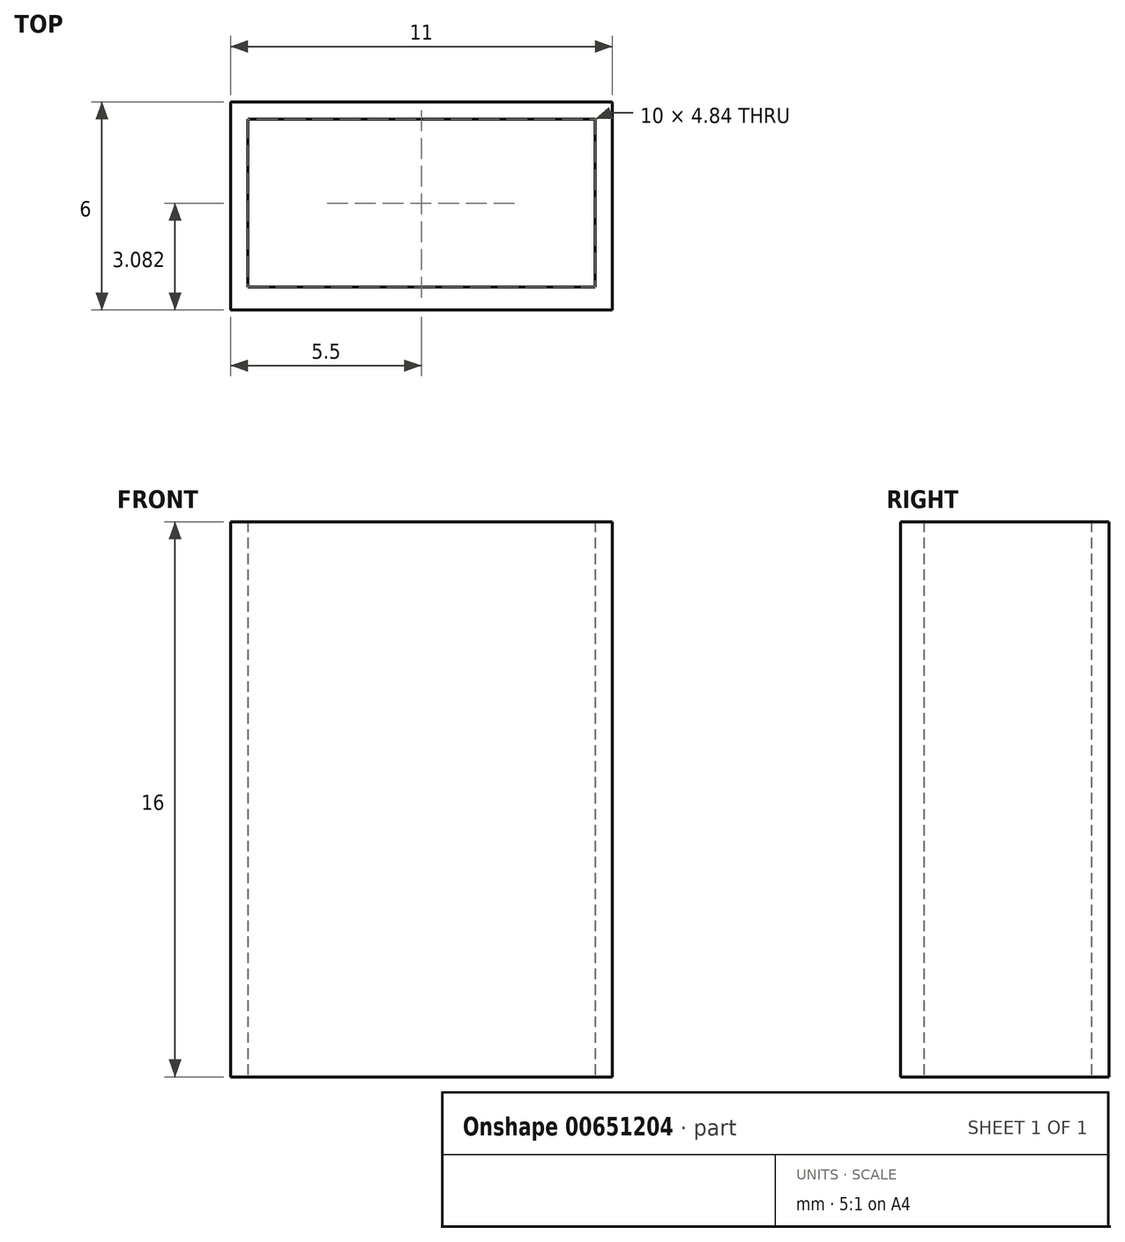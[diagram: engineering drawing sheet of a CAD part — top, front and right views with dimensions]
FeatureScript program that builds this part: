
annotation { "Feature Type Name" : "Feature", "Feature Type Description" : "" }
export const myFeature = defineFeature(function(context is Context, id is Id, definition is map)
    precondition{}
    {
        {
            var Q0;
            Q0=qCreatedBy(makeId("Top.planeOp"),FACE);
            var sketch = newSketch(context, id + "F0", { "sketchPlane" : qUnion([Q0])});
            skLineSegment(sketch, "E0.bottom", {"start": v(-5.5, -3) * mm, "end": v(5.5, -3) * mm});
            skLineSegment(sketch, "E0.top", {"start": v(-5.5, 3) * mm, "end": v(5.5, 3) * mm});
            skLineSegment(sketch, "E0.left", {"start": v(-5.5, -3) * mm, "end": v(-5.5, 3) * mm});
            skLineSegment(sketch, "E0.right", {"start": v(5.5, -3) * mm, "end": v(5.5, 3) * mm});
            skLineSegment(sketch, "E1.bottom", {"start": v(-5, -2.34) * mm, "end": v(5, -2.34) * mm});
            skLineSegment(sketch, "E1.top", {"start": v(-5, 2.5) * mm, "end": v(5, 2.5) * mm});
            skLineSegment(sketch, "E1.left", {"start": v(-5, -2.34) * mm, "end": v(-5, 2.5) * mm});
            skLineSegment(sketch, "E1.right", {"start": v(5, -2.34) * mm, "end": v(5, 2.5) * mm});
            skSolve(sketch);
        }
        {
            var Q0;
            Q0=makeQuery(id+"F0.imprint","IMPRINT",FACE,{"disambiguationData":[TD([[makeQuery(id+"F0.imprint","IMPRINT",EDGE,{"derivedFrom":sQuery(id+"F0.wireOp",EDGE,"E0.bottom")}),1.0]])]});
            extrude(context, id + "F1", {"entities" : qUnion([Q0]), "depth" : 15 * mm, "offsetDistance" : 25 * mm});
        }
        {
            var Q0;
            Q0=makeQuery(id+"F1.opExtrude","CAP_FACE",FACE,{"disambiguationData":[OSD([sQuery(id+"F0.wireOp",EDGE,"E0.bottom"),sQuery(id+"F0.wireOp",EDGE,"E0.top"),sQuery(id+"F0.wireOp",EDGE,"E0.left"),sQuery(id+"F0.wireOp",EDGE,"E0.right"),sQuery(id+"F0.wireOp",EDGE,"E1.bottom"),sQuery(id+"F0.wireOp",EDGE,"E1.top"),sQuery(id+"F0.wireOp",EDGE,"E1.left"),sQuery(id+"F0.wireOp",EDGE,"E1.right")])],"isStart":true});
            extrude(context, id + "F2", {"entities" : qUnion([Q0]), "operationType" : NewBodyOperationType.ADD, "depth" : 1 * mm, "offsetDistance" : 25 * mm});
        }
    });
